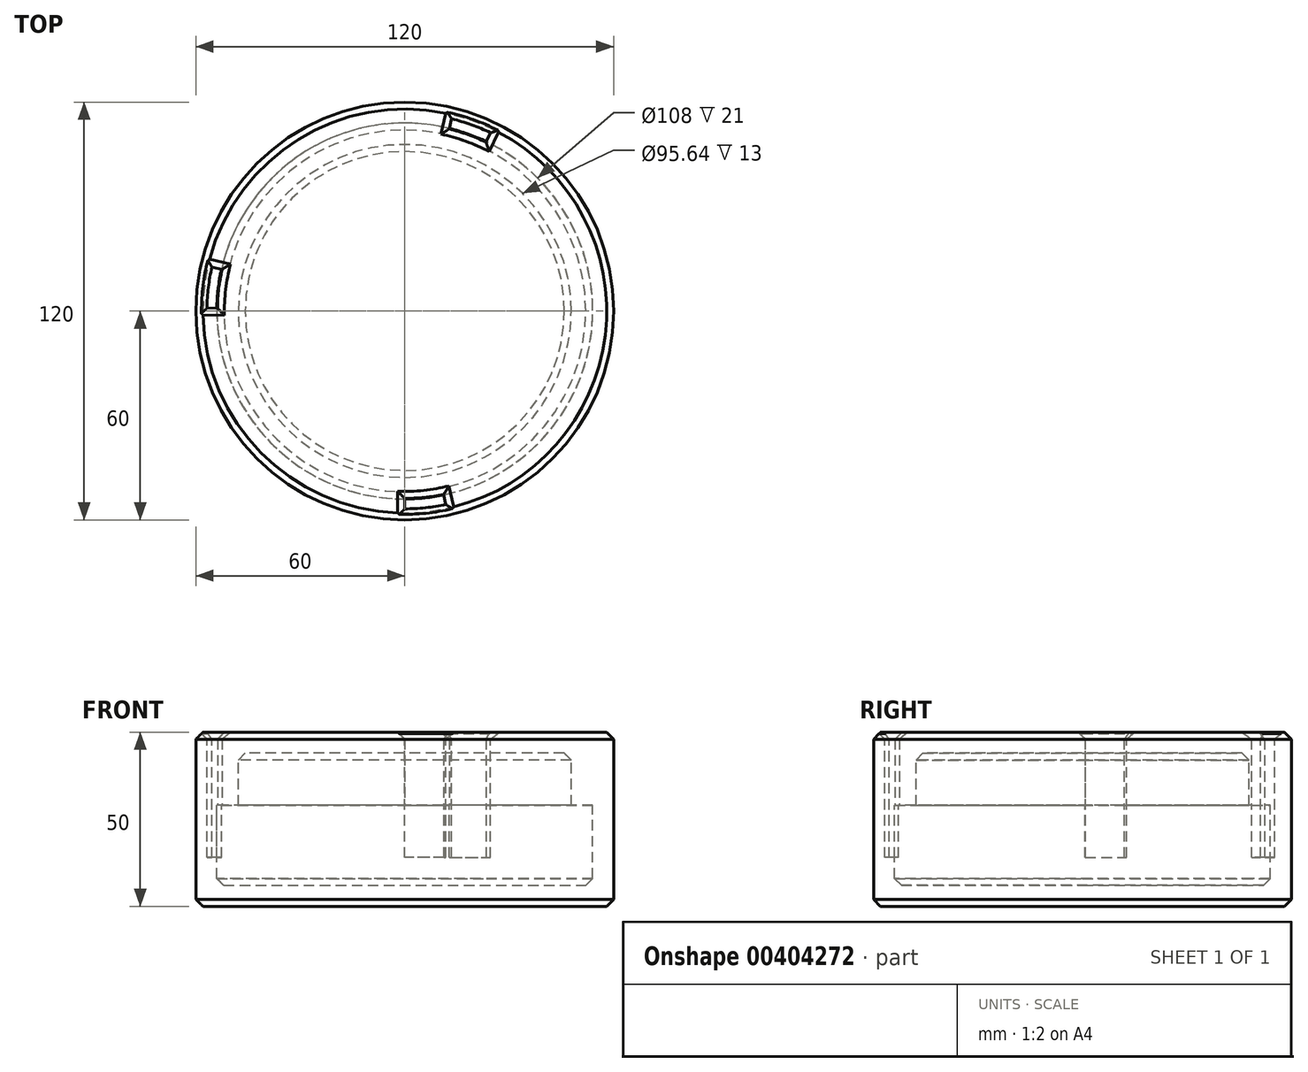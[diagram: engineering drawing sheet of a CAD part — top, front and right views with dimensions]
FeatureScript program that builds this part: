
annotation { "Feature Type Name" : "Feature", "Feature Type Description" : "" }
export const myFeature = defineFeature(function(context is Context, id is Id, definition is map)
    precondition{}
    {
        {
            var Q0;
            Q0=qCreatedBy(makeId("Front.planeOp"),FACE);
            var sketch = newSketch(context, id + "F0", { "sketchPlane" : qUnion([Q0])});
            skLineSegment(sketch, "E0.bottom", {"start": v(60, 0) * mm, "end": v(0, 0) * mm});
            skLineSegment(sketch, "E0.top", {"start": v(60, 50) * mm, "end": v(0, 50) * mm});
            skLineSegment(sketch, "E0.left", {"start": v(60, 0) * mm, "end": v(60, 29) * mm});
            skLineSegment(sketch, "E0.right", {"start": v(-60, 0) * mm, "end": v(-60, 50) * mm, "construction": true});
            skPoint(sketch, "E0.middle", {"position": v(0, 25) * mm});
            skLineSegment(sketch, "E1", {"start": v(0, 50) * mm, "end": v(0, 0) * mm});
            skLineSegment(sketch, "E2", {"start": v(0, 50) * mm, "end": v(-60, 50) * mm, "construction": true});
            skLineSegment(sketch, "E3", {"start": v(0, 0) * mm, "end": v(-60, 0) * mm, "construction": true});
            skLineSegment(sketch, "E4.bottom", {"start": v(60, 44) * mm, "end": v(53.82, 44) * mm});
            skLineSegment(sketch, "E4.top", {"start": v(60, 14) * mm, "end": v(53.82, 14) * mm});
            skLineSegment(sketch, "E4.left", {"start": v(60, 44) * mm, "end": v(60, 29) * mm});
            skLineSegment(sketch, "E4.right", {"start": v(53.82, 44) * mm, "end": v(53.82, 29) * mm});
            skLineSegment(sketch, "E5", {"start": v(60, 29) * mm, "end": v(53.82, 29) * mm});
            skLineSegment(sketch, "E6", {"start": v(0, 44) * mm, "end": v(47.82, 44) * mm});
            skLineSegment(sketch, "E7", {"start": v(47.82, 44) * mm, "end": v(47.82, 29) * mm});
            skLineSegment(sketch, "E8", {"start": v(47.82, 14) * mm, "end": v(53.82, 14) * mm});
            skLineSegment(sketch, "E9", {"start": v(47.82, 29) * mm, "end": v(47.82, 14) * mm});
            skLineSegment(sketch, "E10", {"start": v(53.82, 29) * mm, "end": v(53.82, 14) * mm});
            skLineSegment(sketch, "E11", {"start": v(60, 29) * mm, "end": v(60, 14) * mm});
            skLineSegment(sketch, "E12", {"start": v(60, 29) * mm, "end": v(60, 44) * mm});
            skLineSegment(sketch, "E13", {"start": v(60, 44) * mm, "end": v(60, 50) * mm});
            skLineSegment(sketch, "E14", {"start": v(47.82, 29) * mm, "end": v(0, 29) * mm});
            skLineSegment(sketch, "E15", {"start": v(53.82, 29) * mm, "end": v(47.82, 29) * mm});
            skSolve(sketch);
        }
        {
            var Q0;
            {var subQ1=sQuery(id+"F0.wireOp",EDGE,"E0.top");Q0=makeQuery(id+"F0.imprint","IMPRINT",FACE,{"disambiguationData":[TD([[makeQuery(id+"F0.imprint","IMPRINT",EDGE,{"derivedFrom":subQ1}),1.0]])]});}
            var Q1;
            Q1=sQuery(id+"F0.wireOp",EDGE,"E1");
            revolve(context, id + "F1", {"entities" : qUnion([Q0]), "axis" : qUnion([Q1]), "revolveType" : RevolveType.FULL});
        }
        {
            var Q0;
            {var subQ2=sQuery(id+"F0.wireOp",EDGE,"E0.bottom");Q0=makeQuery(id+"F0.imprint","IMPRINT",FACE,{"disambiguationData":[TD([[makeQuery(id+"F0.imprint","IMPRINT",EDGE,{"derivedFrom":subQ2}),-1.0]])]});}
            var Q1;
            Q1=makeQuery(id+"F0.imprint","IMPRINT",FACE,{"disambiguationData":[TD([[makeQuery(id+"F0.imprint","IMPRINT",EDGE,{"derivedFrom":sQuery(id+"F0.wireOp",EDGE,"E8")}),1.0]])]});
            var Q2;
            Q2=makeQuery(id+"F0.imprint","IMPRINT",FACE,{"disambiguationData":[TD([[makeQuery(id+"F0.imprint","IMPRINT",EDGE,{"derivedFrom":sQuery(id+"F0.wireOp",EDGE,"E4.top")}),-1.0]])]});
            var Q3;
            Q3=sQuery(id+"F0.wireOp",EDGE,"E0.bottom");
            var Q4;
            Q4=sQuery(id+"F0.wireOp",EDGE,"E0.left");
            var Q5;
            Q5=sQuery(id+"F0.wireOp",EDGE,"E5");
            var Q6;
            Q6=sQuery(id+"F0.wireOp",EDGE,"E15");
            var Q7;
            Q7=sQuery(id+"F0.wireOp",EDGE,"E14");
            var Q8;
            Q8=sQuery(id+"F0.wireOp",EDGE,"E1");
            revolve(context, id + "F2", {"entities" : qUnion([Q0, Q1, Q2]), "surfaceEntities" : qUnion([Q3, Q4, Q5, Q6, Q7]), "axis" : qUnion([Q8]), "revolveType" : RevolveType.FULL});
        }
        {
            var Q0;
            Q0=makeQuery(id+"F0.imprint","IMPRINT",FACE,{"disambiguationData":[TD([[makeQuery(id+"F0.imprint","IMPRINT",EDGE,{"derivedFrom":sQuery(id+"F0.wireOp",EDGE,"E4.bottom")}),1.0]])]});
            var Q1;
            Q1=sQuery(id+"F0.wireOp",EDGE,"E1");
            revolve(context, id + "F3", {"entities" : qUnion([Q0]), "axis" : qUnion([Q1]), "revolveType" : RevolveType.FULL});
        }
        {
            var Q0;
            Q0=makeQuery(id+"F2.opRevolve","SWEPT_FACE",FACE,{"disambiguationData":[OSD([sQuery(id+"F0.wireOp",EDGE,"E5"),sQuery(id+"F0.wireOp",EDGE,"E14"),sQuery(id+"F0.wireOp",EDGE,"E15")])]});
            shell(context, id + "F4", {"entities" : qUnion([Q0]), "thickness" : 6 * mm});
        }
        {
            var Q0;
            Q0=makeQuery(id+"F1.opRevolve","SWEPT_FACE",FACE,{"disambiguationData":[OSD([sQuery(id+"F0.wireOp",EDGE,"E15")])]});
            var sketch = newSketch(context, id + "F5", { "sketchPlane" : qUnion([Q0])});
            skCircle(sketch, "E16.0.0", {"center": v(0, 0) * mm, "radius": 47.82 * mm});
            skCircle(sketch, "E17.0.0", {"center": v(0, 0) * mm, "radius": 60 * mm});
            skCircle(sketch, "E18.cCircle", {"center": v(0, 0) * mm, "radius": 47.82 * mm, "construction": true});
            skLineSegment(sketch, "E18.0", {"start": v(0, 47.82) * mm, "end": v(37.39, 29.82) * mm});
            skLineSegment(sketch, "E18.1", {"start": v(37.39, 29.82) * mm, "end": v(46.62, -10.64) * mm});
            skLineSegment(sketch, "E18.2", {"start": v(46.62, -10.64) * mm, "end": v(20.75, -43.09) * mm});
            skLineSegment(sketch, "E18.3", {"start": v(20.75, -43.09) * mm, "end": v(-20.75, -43.09) * mm});
            skLineSegment(sketch, "E18.4", {"start": v(-20.75, -43.09) * mm, "end": v(-46.62, -10.64) * mm});
            skLineSegment(sketch, "E18.5", {"start": v(-46.62, -10.64) * mm, "end": v(-37.39, 29.82) * mm});
            skLineSegment(sketch, "E18.6", {"start": v(-37.39, 29.82) * mm, "end": v(0, 47.82) * mm});
            skLineSegment(sketch, "E19", {"start": v(0, 53.82) * mm, "end": v(0, 0) * mm});
            skLineSegment(sketch, "E20", {"start": v(23.35, -48.5) * mm, "end": v(0, 0) * mm});
            skLineSegment(sketch, "E21", {"start": v(-52.47, -11.98) * mm, "end": v(0, 0) * mm});
            skLineSegment(sketch, "E22", {"start": v(11.2, 52.65) * mm, "end": v(9.94, 46.78) * mm});
            skLineSegment(sketch, "E23", {"start": v(12.76, -52.29) * mm, "end": v(11.34, -46.46) * mm});
            skLineSegment(sketch, "E24", {"start": v(-53.82, -0.8) * mm, "end": v(-47.82, -0.72) * mm});
            skArc(sketch, "E25", {"start": v(11.2, 52.65) * mm, "mid": v(5.63, 53.53) * mm, "end": v(0, 53.82) * mm});
            skArc(sketch, "E26", {"start": v(0, 53.82) * mm, "mid": v(-38.34, 37.77) * mm, "end": v(-53.82, -0.8) * mm});
            skArc(sketch, "E27", {"start": v(-53.82, -0.8) * mm, "mid": v(-53.44, -6.43) * mm, "end": v(-52.47, -11.98) * mm});
            skArc(sketch, "E28", {"start": v(-52.47, -11.98) * mm, "mid": v(-28.3, -45.79) * mm, "end": v(12.76, -52.29) * mm});
            skArc(sketch, "E29", {"start": v(12.76, -52.29) * mm, "mid": v(18.16, -50.67) * mm, "end": v(23.35, -48.5) * mm});
            skArc(sketch, "E30", {"start": v(23.35, -48.5) * mm, "mid": v(53.44, 6.43) * mm, "end": v(11.2, 52.65) * mm});
            skCircle(sketch, "E31", {"center": v(0, 0) * mm, "radius": 56.82 * mm});
            skLineSegment(sketch, "E32", {"start": v(-53.82, -0.8) * mm, "end": v(-56.82, -0.85) * mm});
            skLineSegment(sketch, "E33", {"start": v(-52.47, -11.98) * mm, "end": v(-55.4, -12.64) * mm});
            skLineSegment(sketch, "E34", {"start": v(12.76, -52.29) * mm, "end": v(13.47, -55.2) * mm});
            skLineSegment(sketch, "E35", {"start": v(23.35, -48.5) * mm, "end": v(24.65, -51.2) * mm});
            skLineSegment(sketch, "E36", {"start": v(11.2, 52.65) * mm, "end": v(11.81, 55.58) * mm});
            skLineSegment(sketch, "E37", {"start": v(0, 53.82) * mm, "end": v(0, 56.82) * mm});
            skSolve(sketch);
        }
        {
            var Q0;
            {var subQ3=sQuery(id+"F5.wireOp",EDGE,"E22");Q0=makeQuery(id+"F5.imprint","IMPRINT",FACE,{"disambiguationData":[TD([[makeQuery(id+"F5.imprint","IMPRINT",EDGE,{"derivedFrom":subQ3}),-1.0]])]});}
            var Q1;
            {var subQ3=sQuery(id+"F5.wireOp",EDGE,"E23");Q1=makeQuery(id+"F5.imprint","IMPRINT",FACE,{"disambiguationData":[TD([[makeQuery(id+"F5.imprint","IMPRINT",EDGE,{"derivedFrom":subQ3}),-1.0]])]});}
            var Q2;
            {var subQ3=sQuery(id+"F5.wireOp",EDGE,"E24");Q2=makeQuery(id+"F5.imprint","IMPRINT",FACE,{"disambiguationData":[TD([[makeQuery(id+"F5.imprint","IMPRINT",EDGE,{"derivedFrom":subQ3}),-1.0]])]});}
            extrude(context, id + "F6", {"entities" : qUnion([Q0, Q1, Q2]), "operationType" : NewBodyOperationType.ADD, "depth" : 15 * mm});
        }
        {
            var Q0;
            Q0=makeQuery(id+"F5.imprint","IMPRINT",FACE,{"disambiguationData":[TD([[makeQuery(id+"F5.imprint","IMPRINT",EDGE,{"derivedFrom":sQuery(id+"F5.wireOp",EDGE,"E25")}),1.0]])]});
            var Q1;
            Q1=makeQuery(id+"F5.imprint","IMPRINT",FACE,{"disambiguationData":[TD([[makeQuery(id+"F5.imprint","IMPRINT",EDGE,{"derivedFrom":sQuery(id+"F5.wireOp",EDGE,"E29")}),1.0]])]});
            var Q2;
            Q2=makeQuery(id+"F5.imprint","IMPRINT",FACE,{"disambiguationData":[TD([[makeQuery(id+"F5.imprint","IMPRINT",EDGE,{"derivedFrom":sQuery(id+"F5.wireOp",EDGE,"E27")}),1.0]])]});
            var Q3;
            Q3=makeQuery(id+"F6.opExtrude","CAP_FACE",FACE,{"disambiguationData":[OSD([sQuery(id+"F5.wireOp",EDGE,"E16.0.0"),sQuery(id+"F5.wireOp",EDGE,"E19"),sQuery(id+"F5.wireOp",EDGE,"E22"),sQuery(id+"F5.wireOp",EDGE,"E25")])],"isStart":false});
            extrude(context, id + "F7", {"entities" : qUnion([Q0, Q1, Q2]), "operationType" : NewBodyOperationType.ADD, "endBound" : BoundingType.UP_TO_SURFACE, "endBoundEntityFace" : qUnion([Q3]), "depth" : 25 * mm, "hasSecondDirection" : true, "secondDirectionOppositeDirection" : false, "secondDirectionDepth" : 9 * mm});
        }
        {
            var Q0;
            Q0=makeQuery(id+"F5.imprint","IMPRINT",FACE,{"disambiguationData":[TD([[makeQuery(id+"F5.imprint","IMPRINT",EDGE,{"derivedFrom":sQuery(id+"F5.wireOp",EDGE,"E27")}),1.0]])]});
            var Q1;
            Q1=makeQuery(id+"F5.imprint","IMPRINT",FACE,{"disambiguationData":[TD([[makeQuery(id+"F5.imprint","IMPRINT",EDGE,{"derivedFrom":sQuery(id+"F5.wireOp",EDGE,"E29")}),1.0]])]});
            var Q2;
            Q2=makeQuery(id+"F5.imprint","IMPRINT",FACE,{"disambiguationData":[TD([[makeQuery(id+"F5.imprint","IMPRINT",EDGE,{"derivedFrom":sQuery(id+"F5.wireOp",EDGE,"E25")}),1.0]])]});
            var Q3;
            {var subQ0=sQuery(id+"F5.wireOp",EDGE,"E27");var subQ1=sQuery(id+"F5.wireOp",EDGE,"E16.0.0");Q3=makeQuery(id+"F7.boolean.opBoolean","MERGE",FACE,{"derivedFrom":[makeQuery(id+"F6.opExtrude","CAP_FACE",FACE,{"disambiguationData":[OSD([subQ1,sQuery(id+"F5.wireOp",EDGE,"E21"),sQuery(id+"F5.wireOp",EDGE,"E24"),subQ0])],"isStart":false}),makeQuery(id+"F7.opExtrude","CAP_FACE",FACE,{"disambiguationData":[OSD([subQ1,sQuery(id+"F5.wireOp",EDGE,"E19"),sQuery(id+"F5.wireOp",EDGE,"E22"),sQuery(id+"F5.wireOp",EDGE,"E25")]),ownerDisambiguation([makeQuery(id+"F5.imprint","IMPRINT",EDGE,{"derivedFrom":subQ0})])],"isStart":false})]});}
            extrude(context, id + "F8", {"entities" : qUnion([Q0, Q1, Q2]), "operationType" : NewBodyOperationType.REMOVE, "endBound" : BoundingType.UP_TO_SURFACE, "endBoundEntityFace" : qUnion([Q3]), "depth" : 25 * mm});
        }
        {
            var Q0;
            Q0=makeQuery(id+"F7.boolean.opBoolean","MERGE",FACE,{"derivedFrom":[makeQuery(id+"F6.opExtrude","SWEPT_FACE",FACE,{"disambiguationData":[OSD([sQuery(id+"F5.wireOp",EDGE,"E19")])]}),makeQuery(id+"F7.opExtrude","SWEPT_FACE",FACE,{"disambiguationData":[OSD([sQuery(id+"F5.wireOp",EDGE,"E37")])]})]});
            var Q1;
            Q1=makeQuery(id+"F7.boolean.opBoolean","MERGE",FACE,{"derivedFrom":[makeQuery(id+"F6.opExtrude","SWEPT_FACE",FACE,{"disambiguationData":[OSD([sQuery(id+"F5.wireOp",EDGE,"E21")])]}),makeQuery(id+"F7.opExtrude","SWEPT_FACE",FACE,{"disambiguationData":[OSD([sQuery(id+"F5.wireOp",EDGE,"E33")])]})]});
            var Q2;
            Q2=makeQuery(id+"F7.boolean.opBoolean","MERGE",FACE,{"derivedFrom":[makeQuery(id+"F6.opExtrude","SWEPT_FACE",FACE,{"disambiguationData":[OSD([sQuery(id+"F5.wireOp",EDGE,"E20")])]}),makeQuery(id+"F7.opExtrude","SWEPT_FACE",FACE,{"disambiguationData":[OSD([sQuery(id+"F5.wireOp",EDGE,"E35")])]})]});
            var Q3;
            Q3=sQuery(id+"F0.wireOp",EDGE,"E1");
            revolve(context, id + "F9", {"operationType" : NewBodyOperationType.REMOVE, "entities" : qUnion([Q0, Q1, Q2]), "axis" : qUnion([Q3]), "revolveType" : RevolveType.ONE_DIRECTION, "oppositeDirection" : true, "angle" : 24 * degree});
        }
        {
            var Q0;
            Q0=makeQuery(id+"F5.imprint","IMPRINT",FACE,{"disambiguationData":[TD([[makeQuery(id+"F5.imprint","IMPRINT",EDGE,{"derivedFrom":sQuery(id+"F5.wireOp",EDGE,"E29")}),1.0]])]});
            var Q1;
            Q1=makeQuery(id+"F5.imprint","IMPRINT",FACE,{"disambiguationData":[TD([[makeQuery(id+"F5.imprint","IMPRINT",EDGE,{"derivedFrom":sQuery(id+"F5.wireOp",EDGE,"E27")}),1.0]])]});
            var Q2;
            Q2=makeQuery(id+"F5.imprint","IMPRINT",FACE,{"disambiguationData":[TD([[makeQuery(id+"F5.imprint","IMPRINT",EDGE,{"derivedFrom":sQuery(id+"F5.wireOp",EDGE,"E25")}),1.0]])]});
            extrude(context, id + "F10", {"entities" : qUnion([Q0, Q1, Q2]), "operationType" : NewBodyOperationType.REMOVE, "endBound" : BoundingType.THROUGH_ALL, "oppositeDirection" : true, "depth" : 25 * mm});
        }
        {
            var Q0;
            Q0=makeQuery(id+"F2.opRevolve","SWEPT_EDGE",EDGE,{"disambiguationData":[OSD([sQuery(id+"F0.wireOp",EDGE,"E0.bottom"),sQuery(id+"F0.wireOp",EDGE,"E0.left")])]});
            var Q1;
            Q1=makeQuery(id+"F1.opRevolve","SWEPT_FACE",FACE,{"disambiguationData":[OSD([sQuery(id+"F0.wireOp",EDGE,"E0.top")])]});
            var Q2;
            Q2=makeQuery(id+"F1.opRevolve","SWEPT_EDGE",EDGE,{"disambiguationData":[OSD([sQuery(id+"F0.wireOp",EDGE,"E4.bottom"),sQuery(id+"F0.wireOp",EDGE,"E12"),sQuery(id+"F0.wireOp",EDGE,"E13")])]});
            var Q3;
            Q3=makeQuery(id+"F3.opRevolve","SWEPT_EDGE",EDGE,{"disambiguationData":[OSD([sQuery(id+"F0.wireOp",EDGE,"E4.bottom"),sQuery(id+"F0.wireOp",EDGE,"E12"),sQuery(id+"F0.wireOp",EDGE,"E13")])]});
            var Q4;
            Q4=makeQuery(id+"F3.opRevolve","SWEPT_EDGE",EDGE,{"disambiguationData":[OSD([sQuery(id+"F0.wireOp",EDGE,"E5"),sQuery(id+"F0.wireOp",EDGE,"E11"),sQuery(id+"F0.wireOp",EDGE,"E12")])]});
            var Q5;
            Q5=makeQuery(id+"F4.opShell","OFFSET_EDGE",EDGE,{"disambiguationData":[OSD([sQuery(id+"F0.wireOp",EDGE,"E0.bottom"),sQuery(id+"F0.wireOp",EDGE,"E0.left")])]});
            var Q6;
            Q6=makeQuery(id+"F1.opRevolve","SWEPT_FACE",FACE,{"disambiguationData":[OSD([sQuery(id+"F0.wireOp",EDGE,"E6")])]});
            chamfer(context, id + "F11", {"entities" : qUnion([Q0, Q1, Q2, Q3, Q4, Q5, Q6]), "width" : 2 * mm, "tangentPropagation" : true});
        }
    });
